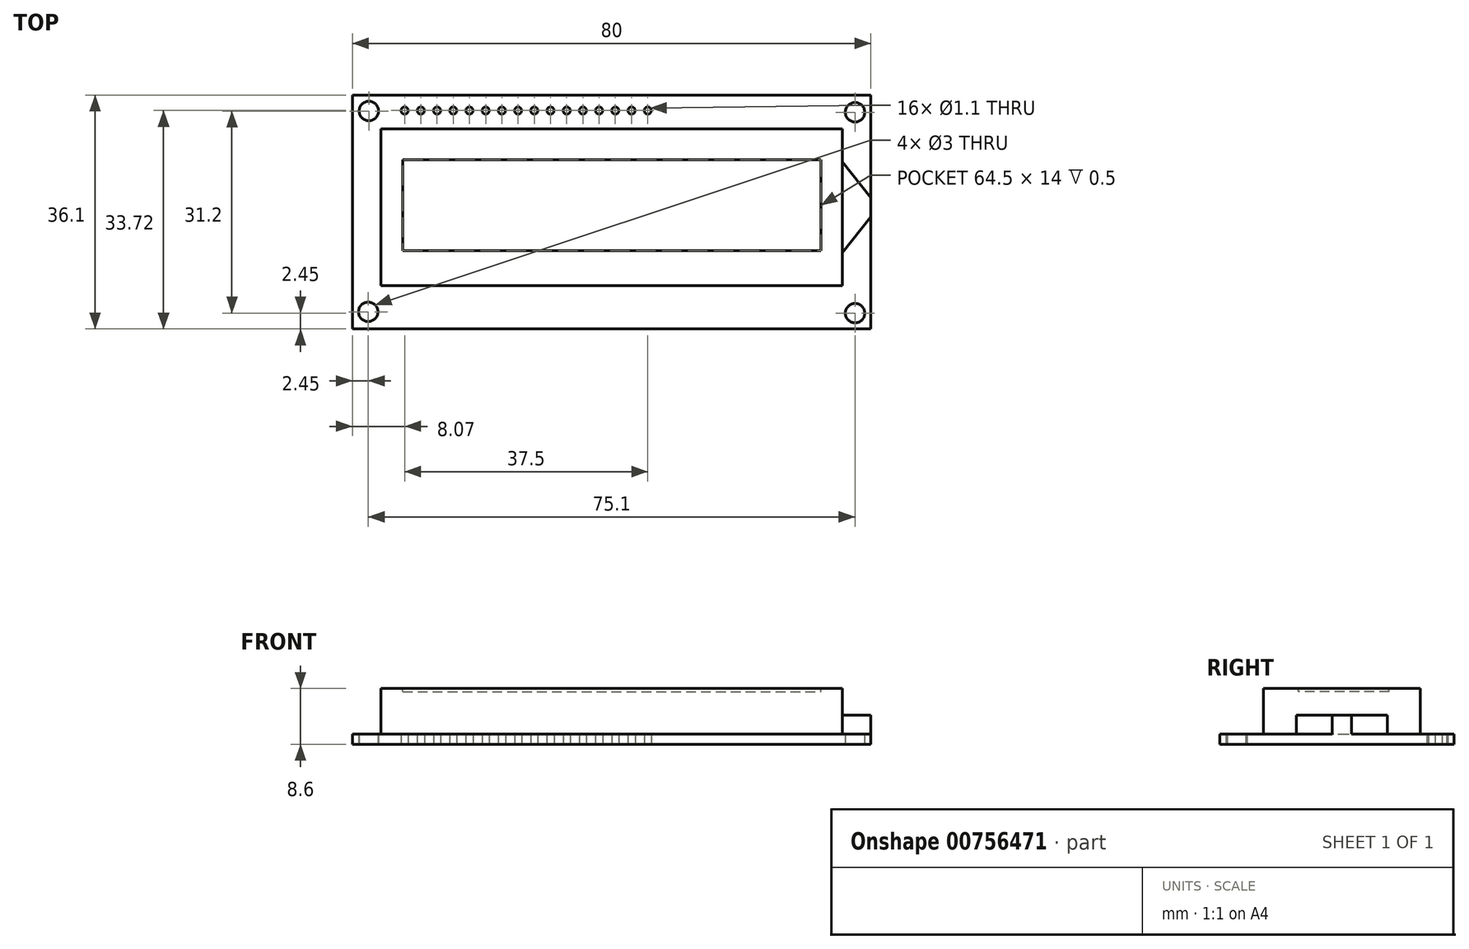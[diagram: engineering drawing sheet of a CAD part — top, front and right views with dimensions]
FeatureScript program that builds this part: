
annotation { "Feature Type Name" : "Feature", "Feature Type Description" : "" }
export const myFeature = defineFeature(function(context is Context, id is Id, definition is map)
    precondition{}
    {
        {
            var Q0;
            Q0=qCreatedBy(makeId("Top.planeOp"),FACE);
            var sketch = newSketch(context, id + "F0", { "sketchPlane" : qUnion([Q0])});
            skLineSegment(sketch, "E0.bottom", {"start": v(-40, -18.05) * mm, "end": v(40, -18.05) * mm});
            skLineSegment(sketch, "E0.top", {"start": v(-40, 18.05) * mm, "end": v(40, 18.05) * mm});
            skLineSegment(sketch, "E0.left", {"start": v(-40, -18.05) * mm, "end": v(-40, 18.05) * mm});
            skLineSegment(sketch, "E0.right", {"start": v(40, -18.05) * mm, "end": v(40, 18.05) * mm});
            skPoint(sketch, "E0.middle", {"position": v(0, 0) * mm});
            skCircle(sketch, "E1", {"center": v(-37.45, 15.6) * mm, "radius": 1.5 * mm});
            skCircle(sketch, "E2", {"center": v(37.55, 15.4) * mm, "radius": 1.5 * mm});
            skCircle(sketch, "E3", {"center": v(-37.55, -15.4) * mm, "radius": 1.5 * mm});
            skCircle(sketch, "E4", {"center": v(37.55, -15.6) * mm, "radius": 1.5 * mm});
            skCircle(sketch, "E5", {"center": v(-31.93, 15.67) * mm, "radius": 0.55 * mm});
            skCircle(sketch, "E6.1.0.0", {"center": v(-29.43, 15.67) * mm, "radius": 0.55 * mm});
            skCircle(sketch, "E6.2.0.0", {"center": v(-26.93, 15.67) * mm, "radius": 0.55 * mm});
            skCircle(sketch, "E6.3.0.0", {"center": v(-24.43, 15.67) * mm, "radius": 0.55 * mm});
            skCircle(sketch, "E6.4.0.0", {"center": v(-21.93, 15.67) * mm, "radius": 0.55 * mm});
            skCircle(sketch, "E6.5.0.0", {"center": v(-19.43, 15.67) * mm, "radius": 0.55 * mm});
            skCircle(sketch, "E6.6.0.0", {"center": v(-16.93, 15.67) * mm, "radius": 0.55 * mm});
            skCircle(sketch, "E6.7.0.0", {"center": v(-14.43, 15.67) * mm, "radius": 0.55 * mm});
            skCircle(sketch, "E6.8.0.0", {"center": v(-11.93, 15.67) * mm, "radius": 0.55 * mm});
            skCircle(sketch, "E6.9.0.0", {"center": v(-9.43, 15.67) * mm, "radius": 0.55 * mm});
            skCircle(sketch, "E6.10.0.0", {"center": v(-6.93, 15.67) * mm, "radius": 0.55 * mm});
            skCircle(sketch, "E6.11.0.0", {"center": v(-4.43, 15.67) * mm, "radius": 0.55 * mm});
            skCircle(sketch, "E6.12.0.0", {"center": v(-1.93, 15.67) * mm, "radius": 0.55 * mm});
            skCircle(sketch, "E6.13.0.0", {"center": v(0.57, 15.67) * mm, "radius": 0.55 * mm});
            skCircle(sketch, "E6.14.0.0", {"center": v(3.07, 15.67) * mm, "radius": 0.55 * mm});
            skCircle(sketch, "E6.15.0.0", {"center": v(5.57, 15.67) * mm, "radius": 0.55 * mm});
            skLineSegment(sketch, "E6.direction1", {"start": v(-31.93, 15.67) * mm, "end": v(-29.43, 15.67) * mm, "construction": true});
            skSolve(sketch);
        }
        {
            var Q0;
            Q0=makeQuery(id+"F0.imprint","IMPRINT",FACE,{"disambiguationData":[TD([[makeQuery(id+"F0.imprint","IMPRINT",EDGE,{"derivedFrom":sQuery(id+"F0.wireOp",EDGE,"E0.bottom")}),1.0]])]});
            extrude(context, id + "F1", {"entities" : qUnion([Q0]), "depth" : 1.6 * mm, "offsetDistance" : 25 * mm});
        }
        {
            var Q0;
            Q0=makeQuery(id+"F1.opExtrude","CAP_FACE",FACE,{"disambiguationData":[OSD([sQuery(id+"F0.wireOp",EDGE,"E0.bottom"),sQuery(id+"F0.wireOp",EDGE,"E0.top"),sQuery(id+"F0.wireOp",EDGE,"E0.left"),sQuery(id+"F0.wireOp",EDGE,"E0.right")])],"isStart":false});
            var sketch = newSketch(context, id + "F2", { "sketchPlane" : qUnion([Q0])});
            skLineSegment(sketch, "E7.bottom", {"start": v(-35.6, -11.35) * mm, "end": v(35.6, -11.35) * mm});
            skLineSegment(sketch, "E7.top", {"start": v(-35.6, 12.85) * mm, "end": v(35.6, 12.85) * mm});
            skLineSegment(sketch, "E7.left", {"start": v(-35.6, -11.35) * mm, "end": v(-35.6, 12.85) * mm});
            skLineSegment(sketch, "E7.right", {"start": v(35.6, -11.35) * mm, "end": v(35.6, 12.85) * mm});
            skPoint(sketch, "E7.middle", {"position": v(0, 0) * mm});
            skLineSegment(sketch, "E8", {"start": v(-35.6, 0.75) * mm, "end": v(-40, 0.75) * mm, "construction": true});
            skPoint(sketch, "E9", {"position": v(-35.6, 7.75) * mm});
            skPoint(sketch, "E10", {"position": v(-40, 2.25) * mm});
            skLineSegment(sketch, "E11", {"start": v(0, -11.35) * mm, "end": v(0, 12.85) * mm, "construction": true});
            skLineSegment(sketch, "E12.MirrorCS", {"start": v(40, 2.25) * mm, "end": v(35.6, 7.75) * mm});
            skLineSegment(sketch, "E13.MirrorCS", {"start": v(40, -0.75) * mm, "end": v(35.6, -6.25) * mm});
            skSolve(sketch);
        }
        {
            var Q0;
            Q0=makeQuery(id+"F2.imprint","IMPRINT",FACE,{"disambiguationData":[TD([[makeQuery(id+"F2.imprint","IMPRINT",EDGE,{"derivedFrom":sQuery(id+"F2.wireOp",EDGE,"E7.bottom")}),1.0]])]});
            extrude(context, id + "F3", {"entities" : qUnion([Q0]), "operationType" : NewBodyOperationType.ADD, "depth" : 7 * mm, "offsetDistance" : 25 * mm});
        }
        {
            var Q0;
            Q0 = qSketchRegion(id + "F2", true);
            var Q1;
            {var subQ0=sQuery(id+"F2.wireOp",EDGE,"E12.MirrorCS");Q1=makeQuery(id+"F2.imprint","IMPRINT",FACE,{"disambiguationData":[TD([[makeQuery(id+"F2.imprint","IMPRINT",EDGE,{"derivedFrom":subQ0}),1.0]])]});}
            extrude(context, id + "F4", {"entities" : qUnion([Q0, Q1]), "operationType" : NewBodyOperationType.ADD, "depth" : 2.9 * mm, "offsetDistance" : 25 * mm});
        }
        {
            var Q0;
            Q0=makeQuery(id+"F3.opExtrude","CAP_FACE",FACE,{"disambiguationData":[OSD([sQuery(id+"F2.wireOp",EDGE,"E7.bottom"),sQuery(id+"F2.wireOp",EDGE,"E7.top"),sQuery(id+"F2.wireOp",EDGE,"E7.left"),sQuery(id+"F2.wireOp",EDGE,"E7.right")])],"isStart":false});
            var sketch = newSketch(context, id + "F5", { "sketchPlane" : qUnion([Q0])});
            skLineSegment(sketch, "E14", {"start": v(-32.2, 8.05) * mm, "end": v(32.3, 8.05) * mm});
            skLineSegment(sketch, "E15", {"start": v(-32.2, -5.95) * mm, "end": v(32.3, -5.95) * mm});
            skLineSegment(sketch, "E16", {"start": v(-32.2, 8.05) * mm, "end": v(-32.2, -5.95) * mm});
            skLineSegment(sketch, "E17", {"start": v(32.3, 8.05) * mm, "end": v(32.3, -5.95) * mm});
            skSolve(sketch);
        }
        {
            var Q0;
            Q0=makeQuery(id+"F5.imprint","IMPRINT",FACE,{"disambiguationData":[TD([[makeQuery(id+"F5.imprint","IMPRINT",EDGE,{"derivedFrom":sQuery(id+"F5.wireOp",EDGE,"E14")}),-1.0]])]});
            extrude(context, id + "F6", {"entities" : qUnion([Q0]), "operationType" : NewBodyOperationType.REMOVE, "oppositeDirection" : true, "depth" : .5 * mm, "offsetDistance" : 25 * mm});
        }
    });
